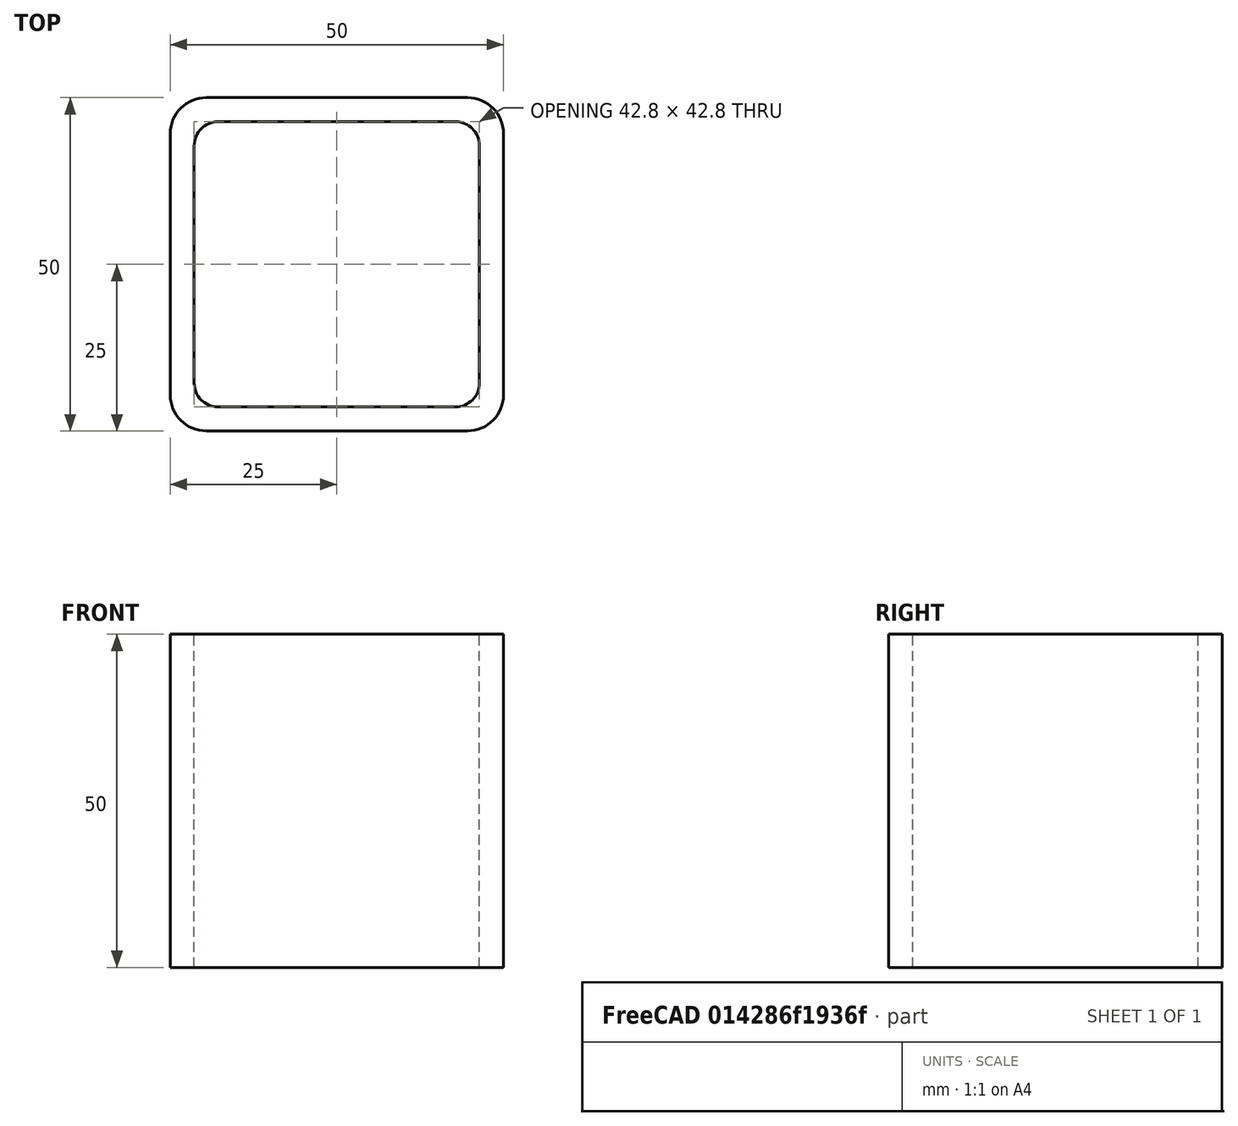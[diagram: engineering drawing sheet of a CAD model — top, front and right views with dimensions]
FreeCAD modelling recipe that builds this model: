
FCSTD DOCUMENT  (FreeCAD 0.15R4671 (Git))
Label: Square hollow section 50x50x3.6 EN10219 S235JRH
License: All rights reserved
LicenseURL: http://en.wikipedia.org/wiki/All_rights_reserved
objects: Sketcher::SketchObject×1, Part::Extrusion×1
note: 2 computed .brp shape members not serialized (recipe doc carries the construction recipe); baked Part::Feature solids carry a one-line shape summary decoded from their .brp

FEATURE [Sketcher::SketchObject] Sketch
  sketch-geometry (16):
    g0: LineSegment StartX=-17.8 StartY=21.4 StartZ=0 EndX=17.8 EndY=21.4 EndZ=0
    g1: LineSegment StartX=21.4 StartY=17.8 StartZ=0 EndX=21.4 EndY=-17.8 EndZ=0
    g2: LineSegment StartX=17.8 StartY=-21.4 StartZ=0 EndX=-17.8 EndY=-21.4 EndZ=0
    g3: LineSegment StartX=-21.4 StartY=-17.8 StartZ=0 EndX=-21.4 EndY=17.8 EndZ=0
    g4: LineSegment StartX=-19.6 StartY=25 StartZ=0 EndX=19.6 EndY=25 EndZ=0
    g5: LineSegment StartX=25 StartY=19.6 StartZ=0 EndX=25 EndY=-19.6 EndZ=0
    g6: LineSegment StartX=19.6 StartY=-25 StartZ=0 EndX=-19.6 EndY=-25 EndZ=0
    g7: LineSegment StartX=-25 StartY=-19.6 StartZ=0 EndX=-25 EndY=19.6 EndZ=0
    g8: ArcOfCircle CenterX=-17.8 CenterY=17.8 CenterZ=0 NormalX=0 NormalY=0 NormalZ=1 Radius=3.6 StartAngle=1.5708 EndAngle=3.14159
    g9: ArcOfCircle CenterX=17.8 CenterY=17.8 CenterZ=0 NormalX=0 NormalY=0 NormalZ=1 Radius=3.6 StartAngle=0 EndAngle=1.5708
    g10: ArcOfCircle CenterX=17.8 CenterY=-17.8 CenterZ=0 NormalX=0 NormalY=0 NormalZ=1 Radius=3.6 StartAngle=4.71239 EndAngle=6.28319
    g11: ArcOfCircle CenterX=-17.8 CenterY=-17.8 CenterZ=0 NormalX=0 NormalY=0 NormalZ=1 Radius=3.6 StartAngle=3.14159 EndAngle=4.71239
    g12: ArcOfCircle CenterX=19.6 CenterY=19.6 CenterZ=0 NormalX=0 NormalY=0 NormalZ=1 Radius=5.4 StartAngle=0 EndAngle=1.5708
    g13: ArcOfCircle CenterX=19.6 CenterY=-19.6 CenterZ=0 NormalX=0 NormalY=0 NormalZ=1 Radius=5.4 StartAngle=4.71239 EndAngle=6.28319
    g14: ArcOfCircle CenterX=-19.6 CenterY=-19.6 CenterZ=0 NormalX=0 NormalY=0 NormalZ=1 Radius=5.4 StartAngle=3.14159 EndAngle=4.71239
    g15: ArcOfCircle CenterX=-19.6 CenterY=19.6 CenterZ=0 NormalX=0 NormalY=0 NormalZ=1 Radius=5.4 StartAngle=1.5708 EndAngle=3.14159
  constraints (36):
    c: Horizontal(g2)
    c: Vertical(g3)
    c: Horizontal(g6)
    c: Vertical(g7)
    c: Tangent(g3,g8) = 1.5708
    c: Tangent(g0,g8) = 1.5708
    c: Tangent(g0,g9) = 1.5708
    c: Tangent(g1,g9) = 1.5708
    c: Tangent(g1,g10) = 1.5708
    c: Tangent(g2,g10) = 1.5708
    c: Tangent(g2,g11) = 1.5708
    c: Tangent(g3,g11) = 1.5708
    c: Tangent(g4,g12) = 1.5708
    c: Tangent(g5,g12) = 1.5708
    c: Tangent(g5,g13) = 1.5708
    c: Tangent(g6,g13) = 1.5708
    c: Tangent(g6,g14) = 1.5708
    c: Tangent(g7,g14) = 1.5708
    c: Tangent(g7,g15) = 1.5708
    c: Tangent(g4,g15) = 1.5708
    c: Equal(g9,g8)
    c: Equal(g9,g11)
    c: Equal(g9,g10)
    c: Equal(g12,g15)
    c: Equal(g12,g14)
    c: Equal(g12,g13)
    c: Symmetric(g4,g6,g-1)
    c: Symmetric(g7,g5,g-2)
    c: DistanceY(g4,g6) = -50
    c: DistanceX(g7,g5) = 50
    c: Symmetric(g3,g1,g-2)
    c: Symmetric(g0,g2,g-1)
    c: DistanceY(g0,g4) = 3.6
    c: DistanceX(g5,g1) = -3.6
    c: Radius(g9) = 3.6
    c: Radius(g12) = 5.4
FEATURE [Part::Extrusion] Extrude  label="Square hollow section 50x50x3.6 EN10219 S235JRH"
  Base = -> Sketch
  Dir = (0,0,50)
  Solid = true
